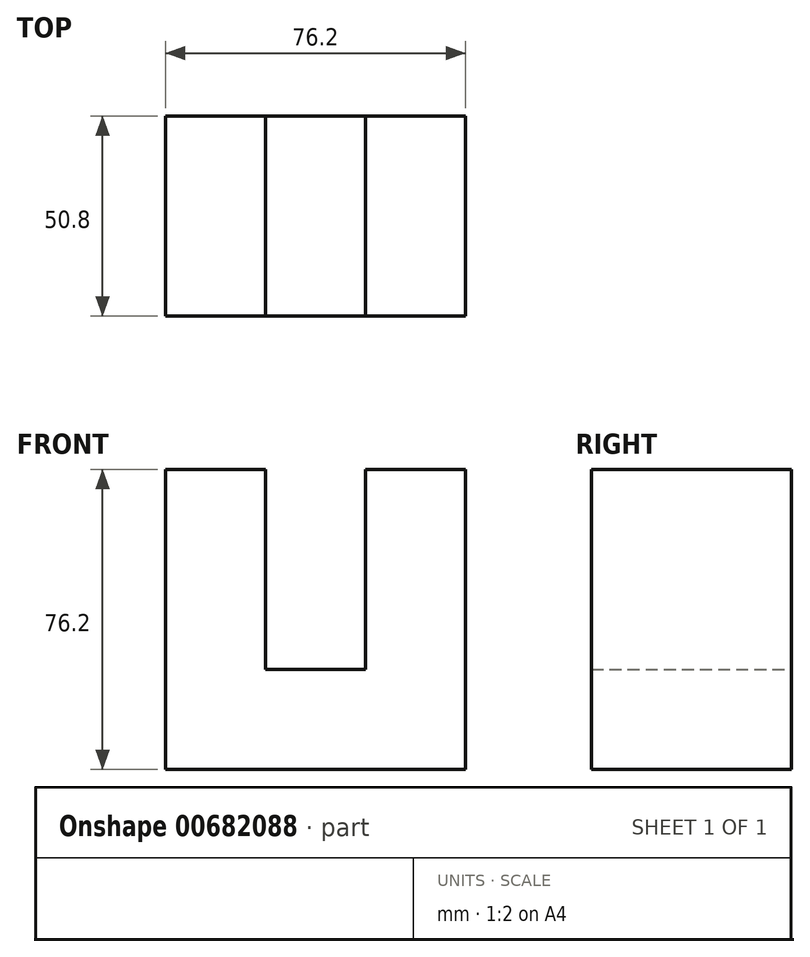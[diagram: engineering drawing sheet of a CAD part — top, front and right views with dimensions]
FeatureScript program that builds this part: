
annotation { "Feature Type Name" : "Feature", "Feature Type Description" : "" }
export const myFeature = defineFeature(function(context is Context, id is Id, definition is map)
    precondition{}
    {
        {
            var Q0;
            Q0=qCreatedBy(makeId("Front.planeOp"),FACE);
            var sketch = newSketch(context, id + "F0", { "sketchPlane" : qUnion([Q0])});
            skLineSegment(sketch, "E0", {"start": v(0, 0) * mm, "end": v(-76.2, 0) * mm});
            skLineSegment(sketch, "E1", {"start": v(-76.2, 0) * mm, "end": v(-76.2, 76.2) * mm});
            skLineSegment(sketch, "E2", {"start": v(-76.2, 76.2) * mm, "end": v(-50.8, 76.2) * mm});
            skLineSegment(sketch, "E3", {"start": v(-50.8, 76.2) * mm, "end": v(-50.8, 25.4) * mm});
            skLineSegment(sketch, "E4", {"start": v(-50.8, 25.4) * mm, "end": v(-25.4, 25.4) * mm});
            skLineSegment(sketch, "E5", {"start": v(-25.4, 25.4) * mm, "end": v(-25.4, 76.2) * mm});
            skLineSegment(sketch, "E6", {"start": v(-25.4, 76.2) * mm, "end": v(0, 76.2) * mm});
            skLineSegment(sketch, "E7", {"start": v(0, 76.2) * mm, "end": v(0, 0) * mm});
            skSolve(sketch);
        }
        {
            var Q0;
            Q0 = qSketchRegion(id + "F0", true);
            extrude(context, id + "F1", {"entities" : qUnion([Q0]), "depth" : 50.8 * mm, "offsetDistance" : 25.4 * mm});
        }
    });
